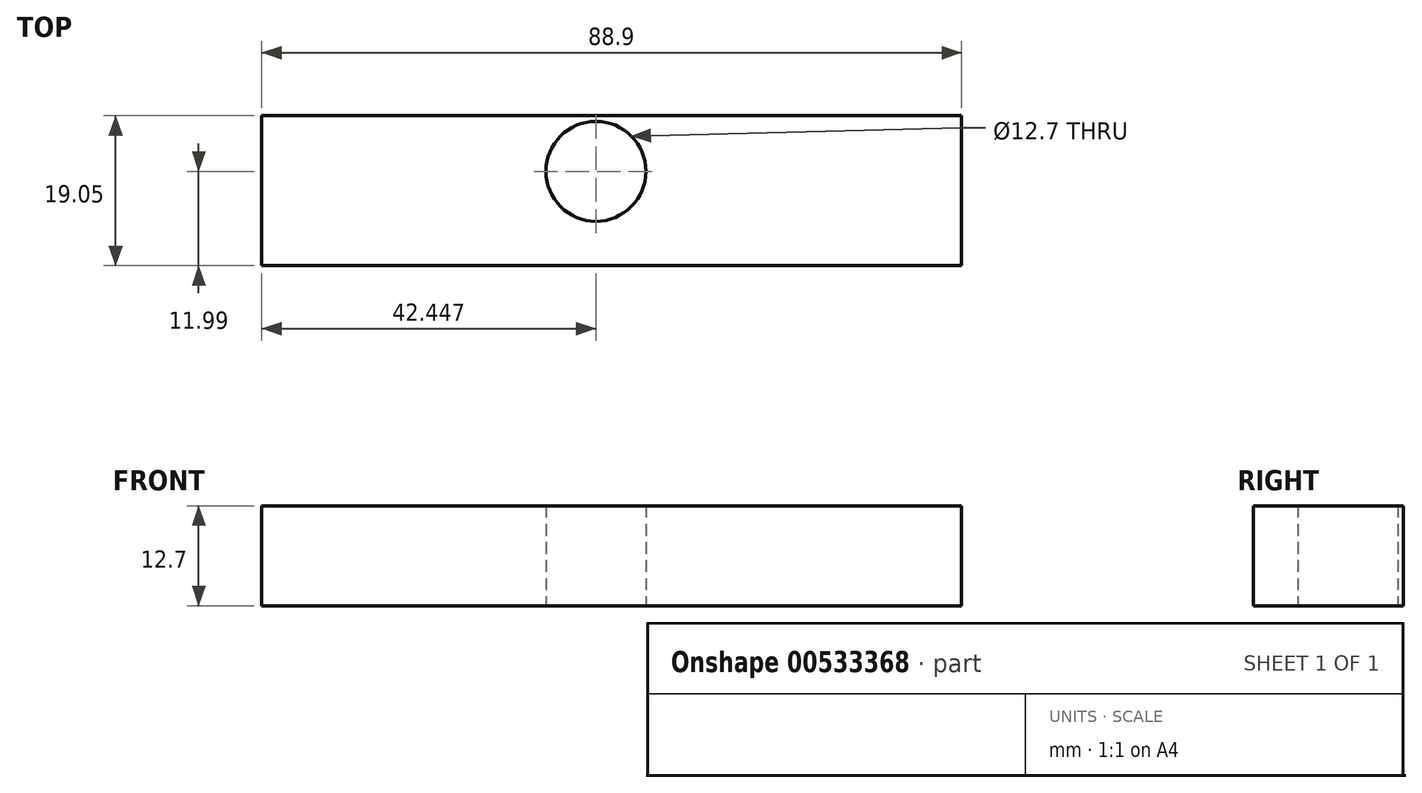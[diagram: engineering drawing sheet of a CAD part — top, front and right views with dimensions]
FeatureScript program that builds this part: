
annotation { "Feature Type Name" : "Feature", "Feature Type Description" : "" }
export const myFeature = defineFeature(function(context is Context, id is Id, definition is map)
    precondition{}
    {
        {
            var Q0;
            Q0=qCreatedBy(makeId("Top.planeOp"),FACE);
            var sketch = newSketch(context, id + "F0", { "sketchPlane" : qUnion([Q0])});
            skLineSegment(sketch, "E0.bottom", {"start": v(-32.9, -12) * mm, "end": v(56, -12) * mm});
            skLineSegment(sketch, "E0.top", {"start": v(-32.9, 7.06) * mm, "end": v(56, 7.06) * mm});
            skLineSegment(sketch, "E0.left", {"start": v(-32.9, -12) * mm, "end": v(-32.9, 7.06) * mm});
            skLineSegment(sketch, "E0.right", {"start": v(56, -12) * mm, "end": v(56, 7.06) * mm});
            skCircle(sketch, "E1", {"center": v(9.56, 0) * mm, "radius": 6.35 * mm});
            skSolve(sketch);
        }
        {
            var Q0;
            Q0 = qSketchRegion(id + "F0", true);
            extrude(context, id + "F1", {"entities" : qUnion([Q0]), "depth" : 12.7 * mm, "offsetDistance" : 25.4 * mm});
        }
    });
